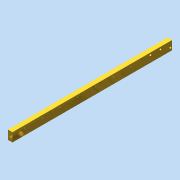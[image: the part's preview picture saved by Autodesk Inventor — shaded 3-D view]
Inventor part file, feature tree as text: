
AUTODESK INVENTOR PART (.ipt)
format: ipt  version: 2016 (Build 200138000, 138)  size: 139,776 bytes
history: native  units: in
note: dims shown in document units (in); Inventor stores cm internally (conversion verified against a paired STEP export)
features: hole x4, pattern_linear x4, sketch x3, extrude x1
ambient origin geometry x8: Origin, YZ Plane, XZ Plane, XY Plane, X Axis, Y Axis, Z Axis, Center Point
bodies: Solid1 (feature_tree)
feature tree (12):
  extrude  "Extrusion1"  Depth=0.5in
  sketch  "Sketch3"  dims[d6=9.0in d7=0.0in d8=0.1344in]
  hole  "Hole1"  [1 undecoded]
  pattern_linear  "Rectangular Pattern1"  Count1=7 Spacing1=1.0in
  sketch  "Sketch6"  dims[d9=0.7in d10=0.067in d11=0.75in d12=0.375in d13=0.25in d14=0.5635in d15=1.0in d16=0.8108in d17=2.7559in d19=1.0in d20=0.75in d23=0.8108in d24=0.5635in d25=0.25in d26=0.375in d27=0.25in d28=0.067in d45=7.793in d46=0.121in d47=0.109in d48=0.75in d49=0.375in d50=0.25in d51=0.5635in d52=0.26in d53=0.8108in d54=1.1811in d56=0.561in d57=0.7874in d59=0.197in d61=0.067in d62=0.75in d63=0.375in d64=0.25in d65=0.5635in d66=0.25in d67=0.8108in d68=2.3in d69=0.15in d70=0.7874in d72=1.0in d73=1.9685in d75=1.5in d76=0.125in d77=0.125in]
  hole  "Hole4"  [1 undecoded]
  pattern_linear  "Rectangular Pattern4"  Spacing1=7.793in  [1 undecoded]
  hole  "Hole5"  [1 undecoded]
  pattern_linear  "Rectangular Pattern5"  Count1=3 Spacing1=0.561in
  pattern_linear  "Rectangular Pattern6"  Spacing1=2.3in  [1 undecoded]
  sketch  "Sketch2"  dims[d3=0.25in d5=0.5in]
  hole  "Hole2"  [1 undecoded]
note: 6 required parameter values undecoded (feature->parameter linkage not recoverable at this tier; creation-order binding heuristic only, values carry confidence <= 0.55)
